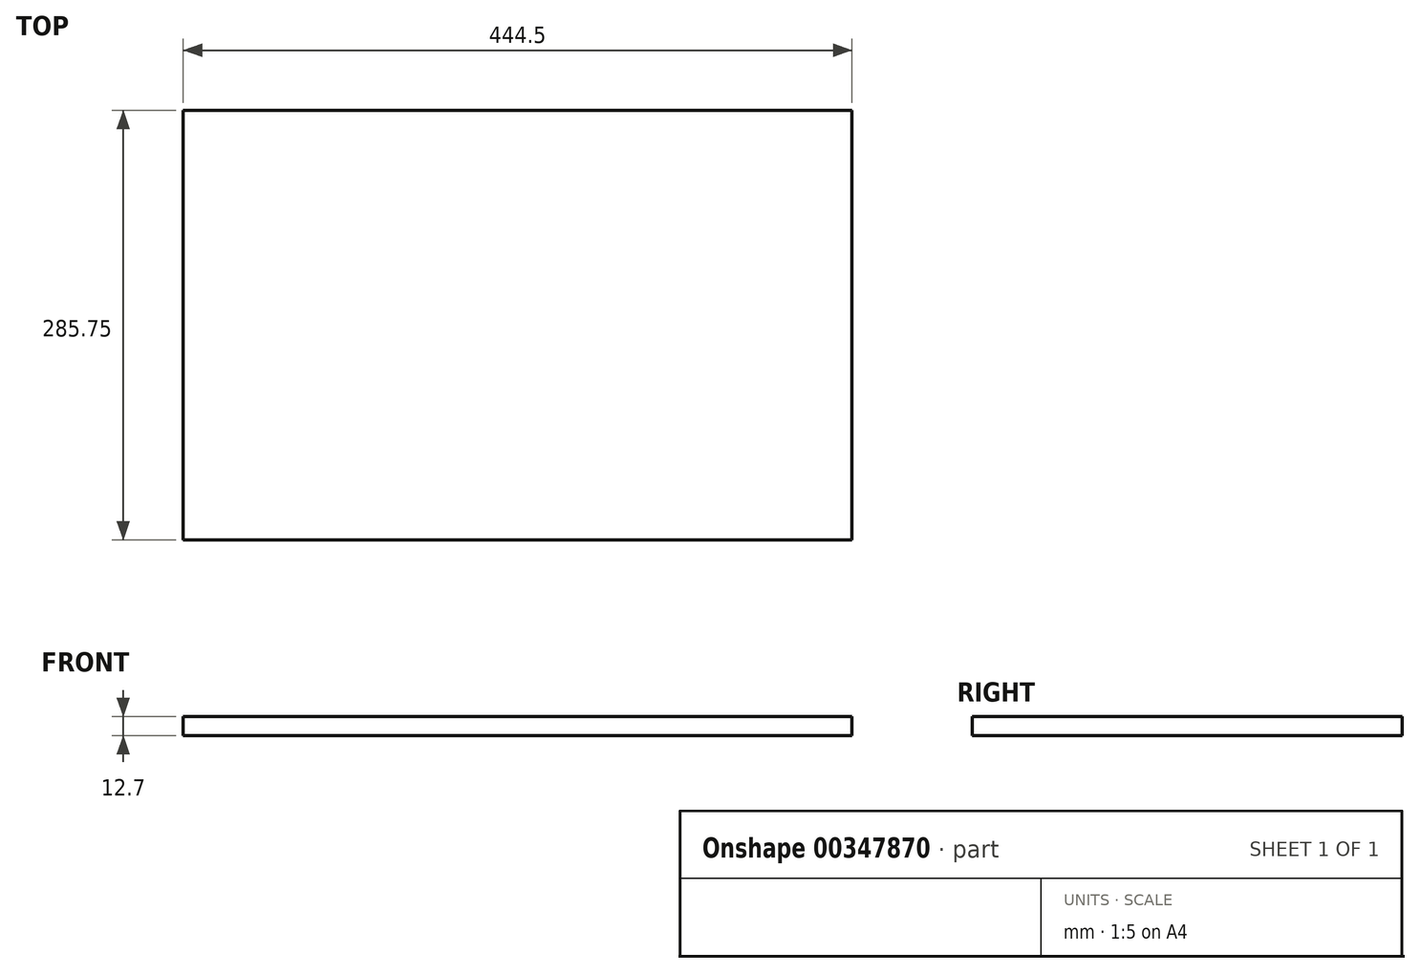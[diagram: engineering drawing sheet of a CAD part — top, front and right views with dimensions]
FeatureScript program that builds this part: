
annotation { "Feature Type Name" : "Feature", "Feature Type Description" : "" }
export const myFeature = defineFeature(function(context is Context, id is Id, definition is map)
    precondition{}
    {
        {
            var Q0;
            Q0=qCreatedBy(makeId("Top.planeOp"),FACE);
            var sketch = newSketch(context, id + "F0", { "sketchPlane" : qUnion([Q0])});
            skLineSegment(sketch, "E0.bottom", {"start": v(0, 0) * mm, "end": v(444.5, 0) * mm});
            skLineSegment(sketch, "E0.top", {"start": v(0, 285.75) * mm, "end": v(444.5, 285.75) * mm});
            skLineSegment(sketch, "E0.left", {"start": v(0, 0) * mm, "end": v(0, 285.75) * mm});
            skLineSegment(sketch, "E0.right", {"start": v(444.5, 0) * mm, "end": v(444.5, 285.75) * mm});
            skSolve(sketch);
        }
        {
            var Q0;
            Q0 = qSketchRegion(id + "F0", true);
            extrude(context, id + "F1", {"entities" : qUnion([Q0]), "depth" : 12.7 * mm});
        }
    });
